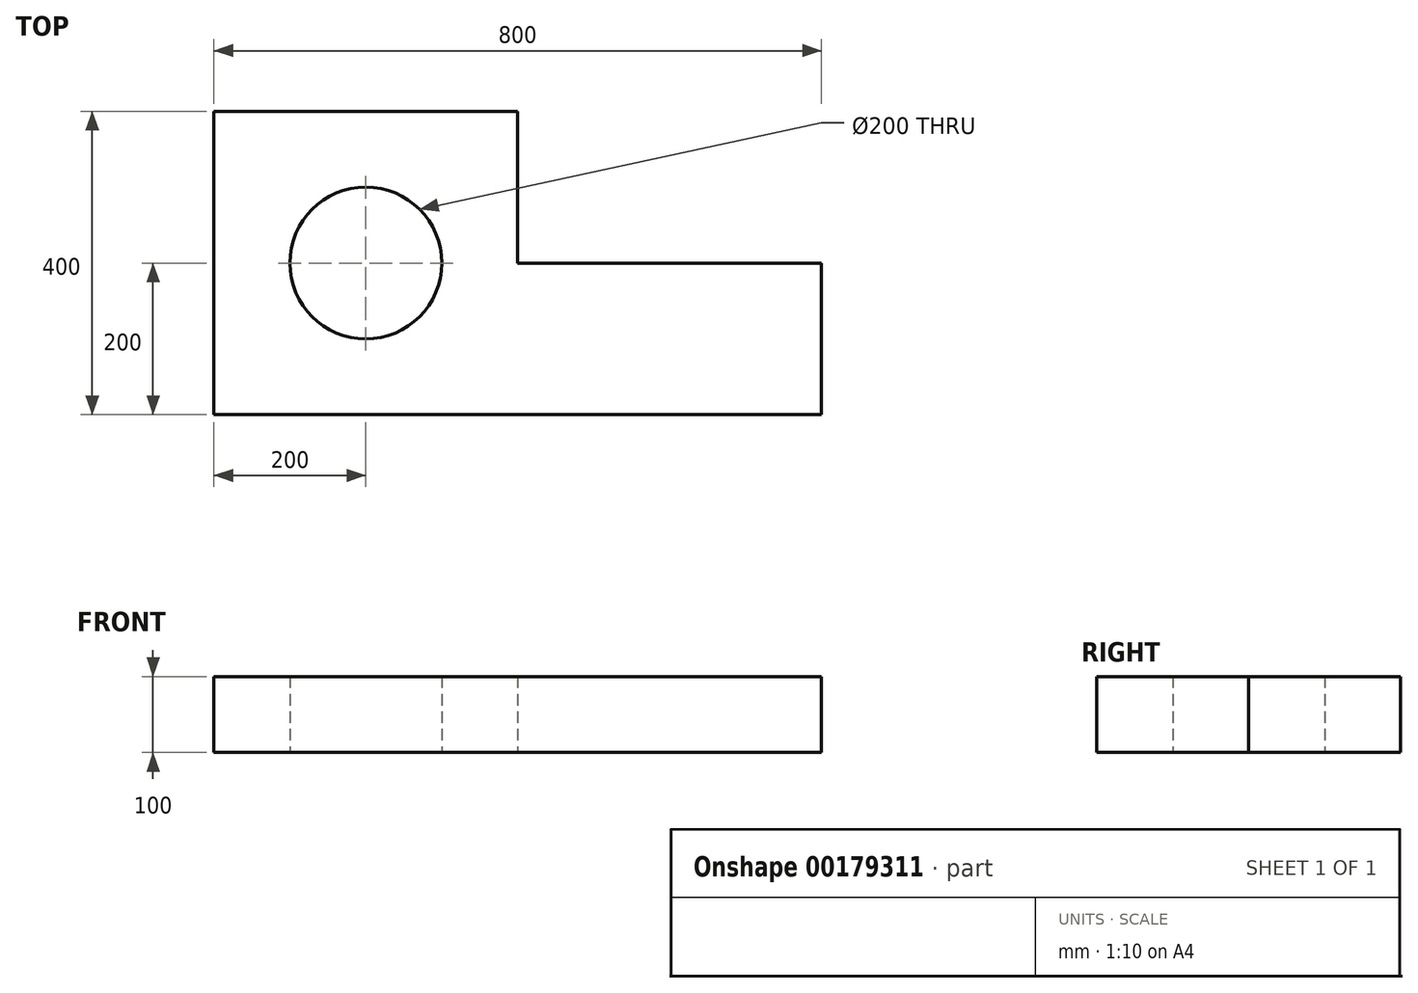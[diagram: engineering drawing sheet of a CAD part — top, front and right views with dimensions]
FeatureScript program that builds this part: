
annotation { "Feature Type Name" : "Feature", "Feature Type Description" : "" }
export const myFeature = defineFeature(function(context is Context, id is Id, definition is map)
    precondition{}
    {
        {
            var Q0;
            Q0=qCreatedBy(makeId("Top.planeOp"),FACE);
            var sketch = newSketch(context, id + "F0", { "sketchPlane" : qUnion([Q0])});
            skLineSegment(sketch, "E0", {"start": v(0, 0) * mm, "end": v(800, 0) * mm});
            skLineSegment(sketch, "E1", {"start": v(800, 0) * mm, "end": v(800, 200) * mm});
            skLineSegment(sketch, "E2", {"start": v(800, 200) * mm, "end": v(400, 200) * mm});
            skLineSegment(sketch, "E3", {"start": v(400, 200) * mm, "end": v(400, 400) * mm});
            skLineSegment(sketch, "E4", {"start": v(400, 400) * mm, "end": v(0, 400) * mm});
            skLineSegment(sketch, "E5", {"start": v(0, 400) * mm, "end": v(0, 0) * mm});
            skLineSegment(sketch, "E6.bottom", {"start": v(0, 200) * mm, "end": v(200, 200) * mm, "construction": true});
            skLineSegment(sketch, "E6.top", {"start": v(0, 400) * mm, "end": v(200, 400) * mm, "construction": true});
            skLineSegment(sketch, "E6.left", {"start": v(0, 200) * mm, "end": v(0, 400) * mm, "construction": true});
            skLineSegment(sketch, "E6.right", {"start": v(200, 200) * mm, "end": v(200, 400) * mm, "construction": true});
            skCircle(sketch, "E7", {"center": v(200, 200) * mm, "radius": 100 * mm});
            skSolve(sketch);
        }
        {
            var Q0;
            Q0=makeQuery(id+"F0.imprint","IMPRINT",FACE,{"disambiguationData":[TD([[makeQuery(id+"F0.imprint","IMPRINT",EDGE,{"derivedFrom":sQuery(id+"F0.wireOp",EDGE,"E0")}),1.0]])]});
            extrude(context, id + "F1", {"entities" : qUnion([Q0]), "depth" : 100 * mm});
        }
    });
